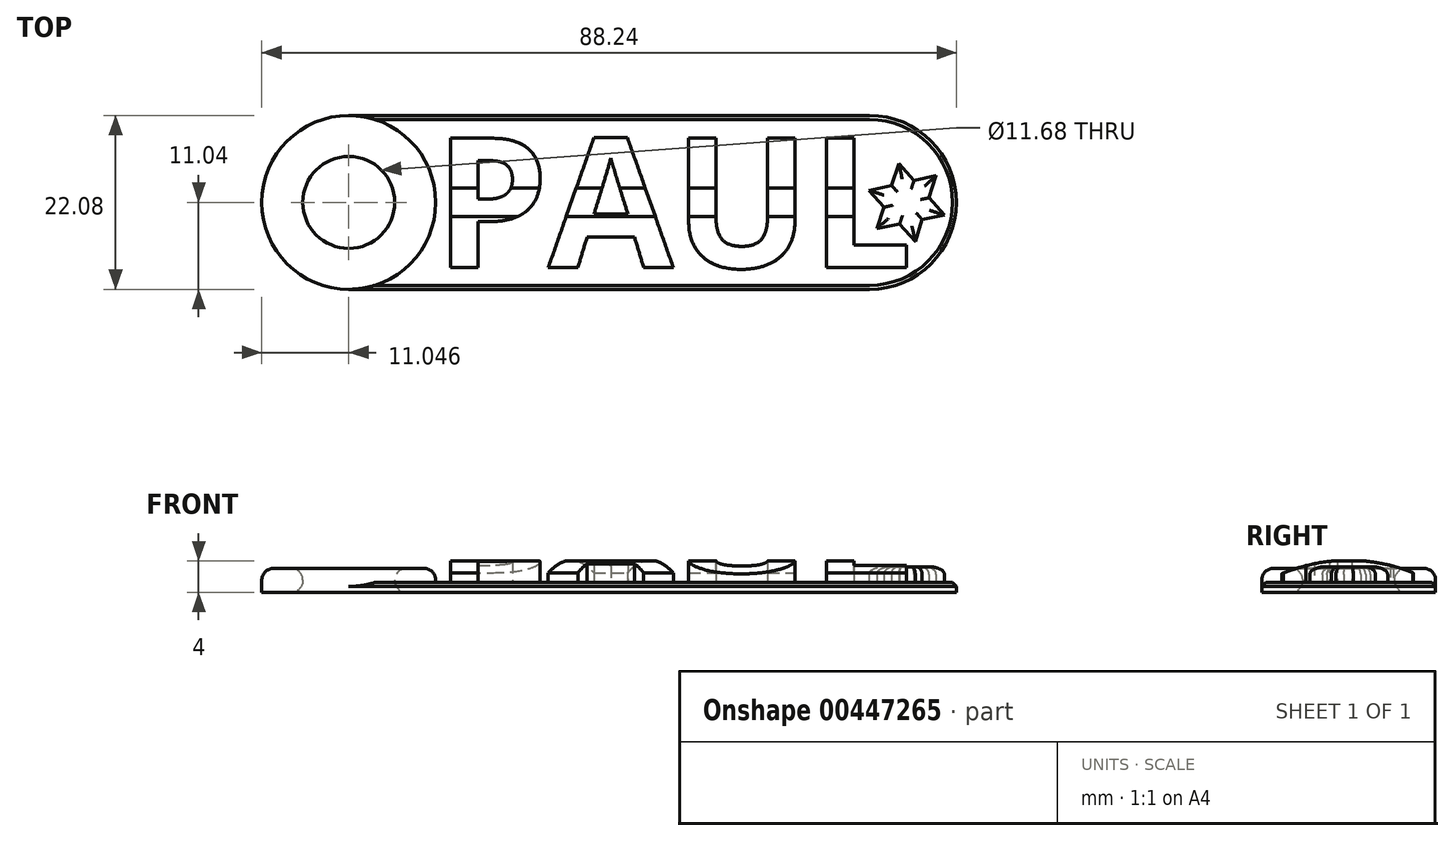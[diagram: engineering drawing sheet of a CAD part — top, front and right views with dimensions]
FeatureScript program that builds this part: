
annotation { "Feature Type Name" : "Feature", "Feature Type Description" : "" }
export const myFeature = defineFeature(function(context is Context, id is Id, definition is map)
    precondition{}
    {
        {
            var Q0;
            Q0=qCreatedBy(makeId("Top.planeOp"),FACE);
            var sketch = newSketch(context, id + "F0", { "sketchPlane" : qUnion([Q0])});
            skArc(sketch, "E0", {"start": v(-36.7, 11.04) * mm, "mid": v(-47.74, 0) * mm, "end": v(-36.7, -11.04) * mm});
            skLineSegment(sketch, "E1", {"start": v(-36.7, 11.04) * mm, "end": v(-36.7, -11.04) * mm, "construction": true});
            skCircle(sketch, "E2", {"center": v(-36.7, 0) * mm, "radius": 5.84 * mm});
            skLineSegment(sketch, "E3", {"start": v(-36.7, 11.04) * mm, "end": v(29.45, 11.04) * mm});
            skLineSegment(sketch, "E4.MirrorCS", {"start": v(-36.7, -11.04) * mm, "end": v(29.45, -11.04) * mm});
            skArc(sketch, "E5", {"start": v(29.45, -11.04) * mm, "mid": v(40.5, 0) * mm, "end": v(29.45, 11.04) * mm});
            skSolve(sketch);
        }
        {
            var Q0;
            Q0 = qSketchRegion(id + "F0", true);
            extrude(context, id + "F1", {"entities" : qUnion([Q0]), "depth" : 1.25 * mm});
        }
        {
            var Q0;
            Q0=qCreatedBy(makeId("Top.planeOp"),FACE);
            var sketch = newSketch(context, id + "F2", { "sketchPlane" : qUnion([Q0])});
            skText(sketch, "E6", { "text": "PAUL", "fontName": "OpenSans-Bold.ttf"});
            const initialGuessF2  = {"E6": [-0.0258, -0.00828, 1, 0, 0.01657]};
            skSetInitialGuess(sketch, initialGuessF2);
            skSolve(sketch);
        }
        {
            var Q0;
            Q0 = qSketchRegion(id + "F2", true);
            extrude(context, id + "F3", {"entities" : qUnion([Q0]), "operationType" : NewBodyOperationType.ADD, "depth" : 4 * mm});
        }
        {
            var Q0;
            Q0=qCreatedBy(makeId("Right.planeOp"),FACE);
            var sketch = newSketch(context, id + "F4", { "sketchPlane" : qUnion([Q0])});
            skArc(sketch, "E7", {"start": v(9.02, 2.13) * mm, "mid": v(0, 4.08) * mm, "end": v(-9.02, 2.13) * mm});
            skLineSegment(sketch, "E8", {"start": v(9.02, 2.13) * mm, "end": v(9.02, 6.53) * mm});
            skLineSegment(sketch, "E9", {"start": v(9.02, 6.53) * mm, "end": v(-9.44, 6.53) * mm});
            skLineSegment(sketch, "E10", {"start": v(-9.44, 6.53) * mm, "end": v(-9.02, 2.13) * mm});
            skSolve(sketch);
        }
        {
            var Q0;
            Q0 = qSketchRegion(id + "F4", true);
            extrude(context, id + "F5", {"entities" : qUnion([Q0]), "operationType" : NewBodyOperationType.REMOVE, "endBound" : BoundingType.SYMMETRIC, "oppositeDirection" : true, "depth" : 100 * mm});
        }
        {
            var Q0;
            {var subQ0=sQuery(id+"F0.wireOp",EDGE,"E3");var subQ1=sQuery(id+"F0.wireOp",EDGE,"E2");var subQ2=sQuery(id+"F0.wireOp",EDGE,"E4.MirrorCS");var subQ3=sQuery(id+"F0.wireOp",EDGE,"E0");var subQ4=sQuery(id+"F0.wireOp",EDGE,"E5");Q0=makeQuery(id+"F3.boolean.opBoolean","SPLIT",FACE,{"disambiguationData":[TD([makeQuery(id+"F1.opExtrude","SWEPT_FACE",FACE,{"disambiguationData":[OSD([subQ3])]})])],"derivedFrom":makeQuery(id+"F1.opExtrude","CAP_FACE",FACE,{"disambiguationData":[OSD([subQ3,subQ1,subQ0,subQ2,subQ4])],"isStart":false})});}
            var sketch = newSketch(context, id + "F6", { "sketchPlane" : qUnion([Q0])});
            skCircle(sketch, "E11", {"center": v(-36.7, 0) * mm, "radius": 5.84 * mm});
            skCircle(sketch, "E12", {"center": v(-36.7, 0) * mm, "radius": 11.04 * mm});
            skSolve(sketch);
        }
        {
            var Q0;
            Q0 = qSketchRegion(id + "F6", true);
            extrude(context, id + "F7", {"entities" : qUnion([Q0]), "operationType" : NewBodyOperationType.ADD, "depth" : 1.8 * mm});
        }
        {
            var Q0;
            Q0=makeQuery(id+"F7.opExtrude","CAP_EDGE",EDGE,{"disambiguationData":[OSD([sQuery(id+"F6.wireOp",EDGE,"E12")])],"isStart":false});
            var Q1;
            Q1=makeQuery(id+"F7.opExtrude","CAP_EDGE",EDGE,{"disambiguationData":[OSD([sQuery(id+"F6.wireOp",EDGE,"E11")])],"isStart":false});
            var Q2;
            Q2=makeQuery(id+"F1.opExtrude","CAP_EDGE",EDGE,{"disambiguationData":[OSD([sQuery(id+"F0.wireOp",EDGE,"E2")])],"isStart":true});
            fillet(context, id + "F8", {"entities" : qUnion([Q0, Q1, Q2]), "radius" : 1.49 * mm, "tangentPropagation" : true, "allowEdgeOverflow" : false});
        }
        {
            var Q0;
            {var subQ0=sQuery(id+"F0.wireOp",EDGE,"E3");var subQ1=sQuery(id+"F0.wireOp",EDGE,"E2");var subQ2=sQuery(id+"F0.wireOp",EDGE,"E4.MirrorCS");var subQ3=sQuery(id+"F0.wireOp",EDGE,"E0");var subQ4=sQuery(id+"F0.wireOp",EDGE,"E5");Q0=makeQuery(id+"F3.boolean.opBoolean","SPLIT",FACE,{"disambiguationData":[TD([makeQuery(id+"F1.opExtrude","SWEPT_FACE",FACE,{"disambiguationData":[OSD([subQ3])]})])],"derivedFrom":makeQuery(id+"F1.opExtrude","CAP_FACE",FACE,{"disambiguationData":[OSD([subQ3,subQ1,subQ0,subQ2,subQ4])],"isStart":false})});}
            var sketch = newSketch(context, id + "F9", { "sketchPlane" : qUnion([Q0])});
            skCircle(sketch, "E13.cCircle", {"center": v(34.2, 0) * mm, "radius": 2.53 * mm, "construction": true});
            skLineSegment(sketch, "E13.0", {"start": v(33.2, 4.96) * mm, "end": v(38.98, -1.63) * mm});
            skLineSegment(sketch, "E13.1", {"start": v(38.98, -1.63) * mm, "end": v(30.4, -3.33) * mm});
            skLineSegment(sketch, "E13.2", {"start": v(30.4, -3.33) * mm, "end": v(33.2, 4.96) * mm});
            skPoint(sketch, "E13.0.midPoint", {"position": v(36.1, 1.67) * mm});
            skLineSegment(sketch, "E14.0", {"start": v(35.27, -4.94) * mm, "end": v(29.38, 1.53) * mm});
            skLineSegment(sketch, "E14.1", {"start": v(29.38, 1.53) * mm, "end": v(37.93, 3.4) * mm});
            skLineSegment(sketch, "E14.2", {"start": v(37.93, 3.4) * mm, "end": v(35.27, -4.94) * mm});
            skPoint(sketch, "E14.0.midPoint", {"position": v(32.32, -1.7) * mm});
            skSolve(sketch);
        }
        {
            var Q0;
            Q0 = qSketchRegion(id + "F9", true);
            extrude(context, id + "F10", {"entities" : qUnion([Q0]), "operationType" : NewBodyOperationType.ADD, "depth" : 2 * mm});
        }
        {
            var Q0;
            Q0=makeQuery(id+"F10.opExtrude","CAP_FACE",FACE,{"disambiguationData":[OSD([sQuery(id+"F9.wireOp",EDGE,"E13.0"),sQuery(id+"F9.wireOp",EDGE,"E13.1"),sQuery(id+"F9.wireOp",EDGE,"E13.2"),sQuery(id+"F9.wireOp",EDGE,"E14.0"),sQuery(id+"F9.wireOp",EDGE,"E14.1"),sQuery(id+"F9.wireOp",EDGE,"E14.2")])],"isStart":false});
            fillet(context, id + "F11", {"entities" : qUnion([Q0]), "radius" : 1 * mm, "tangentPropagation" : true, "allowEdgeOverflow" : false});
        }
        {
            var Q0;
            Q0=makeQuery(id+"F1.opExtrude","CAP_EDGE",EDGE,{"disambiguationData":[OSD([sQuery(id+"F0.wireOp",EDGE,"E4.MirrorCS")])],"isStart":false});
            chamfer(context, id + "F12", {"entities" : qUnion([Q0]), "width" : 0.5 * mm, "tangentPropagation" : true});
        }
    });
